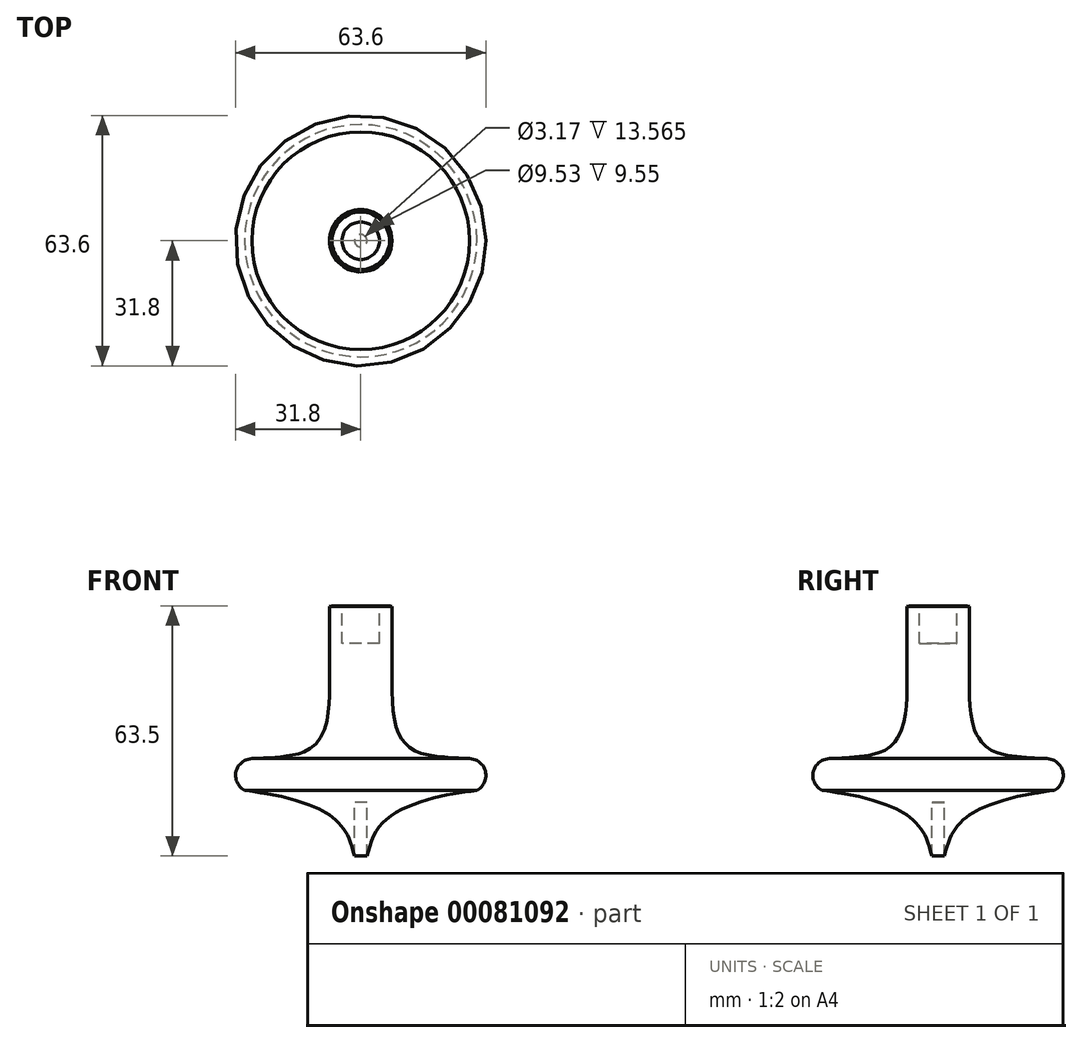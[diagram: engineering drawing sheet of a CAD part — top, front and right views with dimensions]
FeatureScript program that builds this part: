
annotation { "Feature Type Name" : "Feature", "Feature Type Description" : "" }
export const myFeature = defineFeature(function(context is Context, id is Id, definition is map)
    precondition{}
    {
        {
            var Q0;
            Q0=qCreatedBy(makeId("Front.planeOp"),FACE);
            var sketch = newSketch(context, id + "F0", { "sketchPlane" : qUnion([Q0])});
            skLineSegment(sketch, "E0", {"start": v(4.76, 49.94) * mm, "end": v(4.76, 40.38) * mm});
            skLineSegment(sketch, "E1", {"start": v(4.76, 40.38) * mm, "end": v(0, 40.38) * mm});
            skLineSegment(sketch, "E2", {"start": v(4.76, 49.94) * mm, "end": v(7.3, 49.94) * mm});
            skLineSegment(sketch, "E3", {"start": v(1.59, -13.56) * mm, "end": v(1.59, 0) * mm});
            skLineSegment(sketch, "E4", {"start": v(1.59, 0) * mm, "end": v(0, 0) * mm});
            skLineSegment(sketch, "E5", {"start": v(31.75, 6.88) * mm, "end": v(0, 6.88) * mm});
            skArc(sketch, "E6", {"start": v(27.67, 11.15) * mm, "mid": v(31.7, 7.83) * mm, "end": v(29.5, 3.09) * mm});
            skFitSpline(sketch, "E7", {"points": [v(1.59, -13.56) * mm, v(3.99, -7.22) * mm, v(9.58, -2.2) * mm, v(20.2, 1.54) * mm, v(29.5, 3.09) * mm], "startDerivative": vector(8.27, 30.12) * mm, "endDerivative": vector(34.48, 4.59) * mm});
            skLineSegment(sketch, "E8", {"start": v(0, 40.38) * mm, "end": v(0, 0) * mm});
            skFitSpline(sketch, "E9", {"points": [v(27.67, 11.15) * mm, v(22.88, 11.43) * mm, v(14.87, 12.7) * mm, v(10.87, 15.58) * mm, v(8.47, 21.42) * mm, v(7.91, 33.2) * mm, v(7.91, 40.44) * mm], "startDerivative": vector(-31.48, 1.52) * mm, "endDerivative": vector(-0.11, 38.96) * mm});
            skLineSegment(sketch, "E10", {"start": v(7.91, 40.44) * mm, "end": v(7.91, 49.85) * mm});
            skLineSegment(sketch, "E11", {"start": v(7.91, 49.85) * mm, "end": v(7.3, 49.94) * mm});
            skSolve(sketch);
        }
        {
            var Q0;
            Q0=makeQuery(id+"F0.imprint","IMPRINT",FACE,{"disambiguationData":[TD([[makeQuery(id+"F0.imprint","IMPRINT",EDGE,{"derivedFrom":sQuery(id+"F0.wireOp",EDGE,"E0")}),1.0]])]});
            var Q1;
            Q1=sQuery(id+"F0.wireOp",EDGE,"E8");
            revolve(context, id + "F1", {"entities" : qUnion([Q0]), "axis" : qUnion([Q1]), "revolveType" : RevolveType.FULL});
        }
    });
